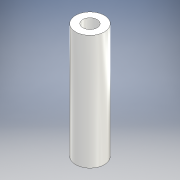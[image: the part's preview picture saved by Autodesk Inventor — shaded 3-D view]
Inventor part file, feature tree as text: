
AUTODESK INVENTOR PART (.ipt)
format: ipt  version: 2020.2 (Build 242310000, 310)  size: 113,664 bytes
history: native  units: mm
features: other x3, extrude x2, sketch x2
ambient origin geometry x8: Origin, YZ Plane, XZ Plane, XY Plane, X Axis, Y Axis, Z Axis, Center Point
bodies: Body1 (feature_tree)
feature tree (7):
  other  "ソリッド1"
  extrude  "押し出し1"  Depth=6.0mm
  other  "作業平面1"
  extrude  "押し出し2"  Depth=3.0mm
  sketch  "スケッチ1"
  sketch  "スケッチ2"
  other  "断面エッジを投影1"
